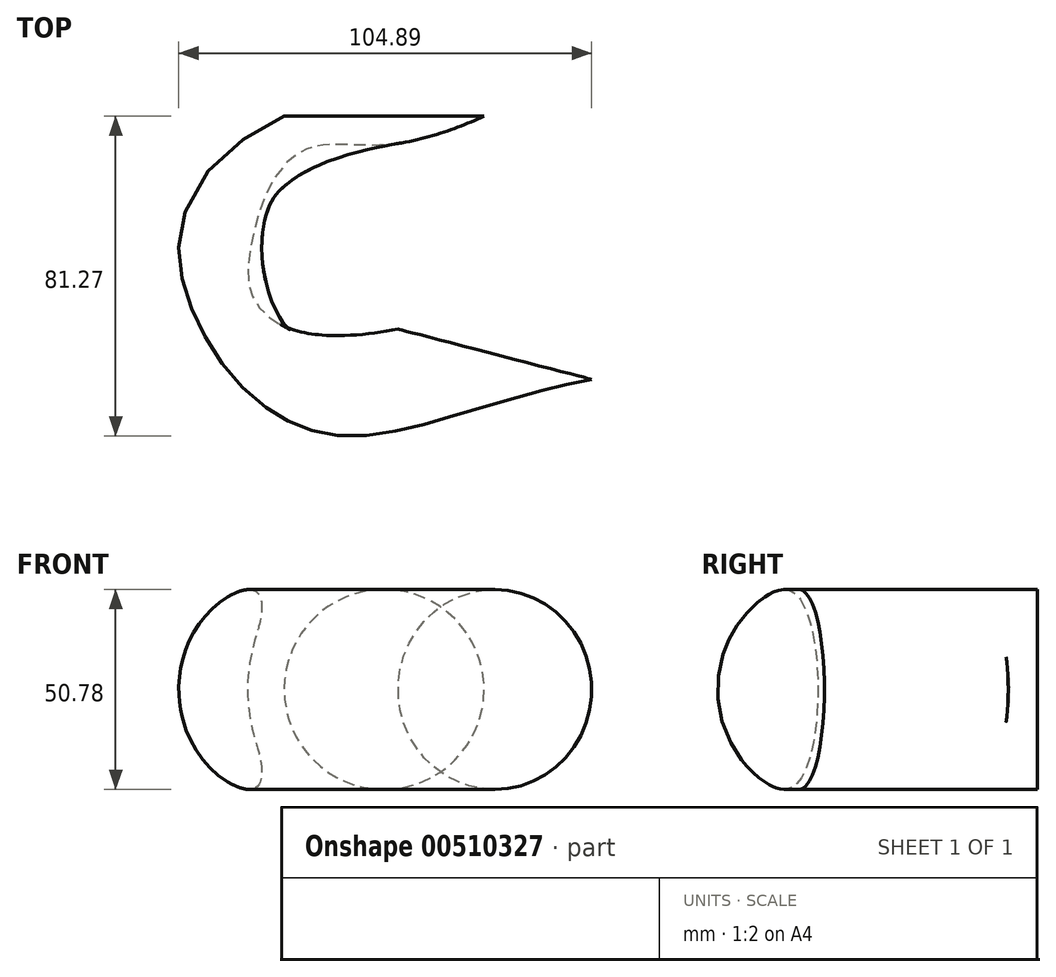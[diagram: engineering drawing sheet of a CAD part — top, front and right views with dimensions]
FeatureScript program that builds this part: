
annotation { "Feature Type Name" : "Feature", "Feature Type Description" : "" }
export const myFeature = defineFeature(function(context is Context, id is Id, definition is map)
    precondition{}
    {
        {
            var Q0;
            Q0=qCreatedBy(makeId("Front.planeOp"),FACE);
            var sketch = newSketch(context, id + "F0", { "sketchPlane" : qUnion([Q0])});
            skCircle(sketch, "E0", {"center": v(0, 0) * mm, "radius": 25.4 * mm});
            skSolve(sketch);
        }
        {
            var Q0;
            Q0=qCreatedBy(makeId("Top.planeOp"),FACE);
            var sketch = newSketch(context, id + "F1", { "sketchPlane" : qUnion([Q0])});
            skFitSpline(sketch, "E1", {"points": [v(0, 0) * mm, v(-33.01, -25.53) * mm, v(-21.95, -59.2) * mm, v(28.13, -60.5) * mm], "startDerivative": vector(-130.6, -61.19) * mm, "endDerivative": vector(157.79, 29.35) * mm});
            skSolve(sketch);
        }
        {
            var Q0;
            Q0=makeQuery(id+"F0.imprint","IMPRINT",FACE,{"disambiguationData":[TD([[makeQuery(id+"F0.imprint","IMPRINT",EDGE,{"derivedFrom":sQuery(id+"F0.wireOp",EDGE,"E0")}),1.0]])]});
            var Q1;
            Q1=sQuery(id+"F1.wireOp",EDGE,"E1");
            sweep(context, id + "F2", {"profiles" : qUnion([Q0]), "path" : qUnion([Q1])});
        }
    });
